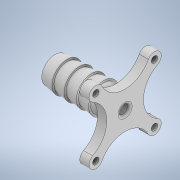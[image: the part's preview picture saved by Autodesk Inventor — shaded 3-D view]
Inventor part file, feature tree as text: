
AUTODESK INVENTOR PART (.ipt)
format: ipt  version: 2020 (Build 240168000, 168)  size: 212,992 bytes
history: native  units: in
note: dims shown in document units (in); Inventor stores cm internally (conversion verified against a paired STEP export)
features: sketch x4, fillet x2, revolve x1, loft x1, extrude x1
ambient origin geometry x8: Origin, YZ Plane, XZ Plane, XY Plane, X Axis, Y Axis, Z Axis, Center Point
bodies: Body1 (feature_tree)
feature tree (9):
  revolve  "Revolution1"  [1 undecoded]
  loft  "Loft1"
  fillet  "Fillet2"  Radius=0.25in
  extrude  "Extrusion3"  Depth=0.125in
  fillet  "Fillet3"  Radius=0.125in
  sketch  "Sketch3"  dims[d4=0.18in d6=0.206in]
  sketch  "Sketch4"  dims[d7=0.1667in d8=0.125in d9=0.25in]
  sketch  "Sketch5"  dims[d10=90.0deg d11=0.286in d15=0.125in]
  sketch  "Sketch6"  dims[d16=0.0in d17=90.0deg d18=0.0in d19=90.0deg d20=0.0312in d21=0.8in d22=0.0866in d23=0.05in d24=1.5748in d26=360.0deg d28=0.125in d29=0.0in d30=0.0312in]
note: 1 required parameter value undecoded (feature->parameter linkage not recoverable at this tier; creation-order binding heuristic only, values carry confidence <= 0.55)
